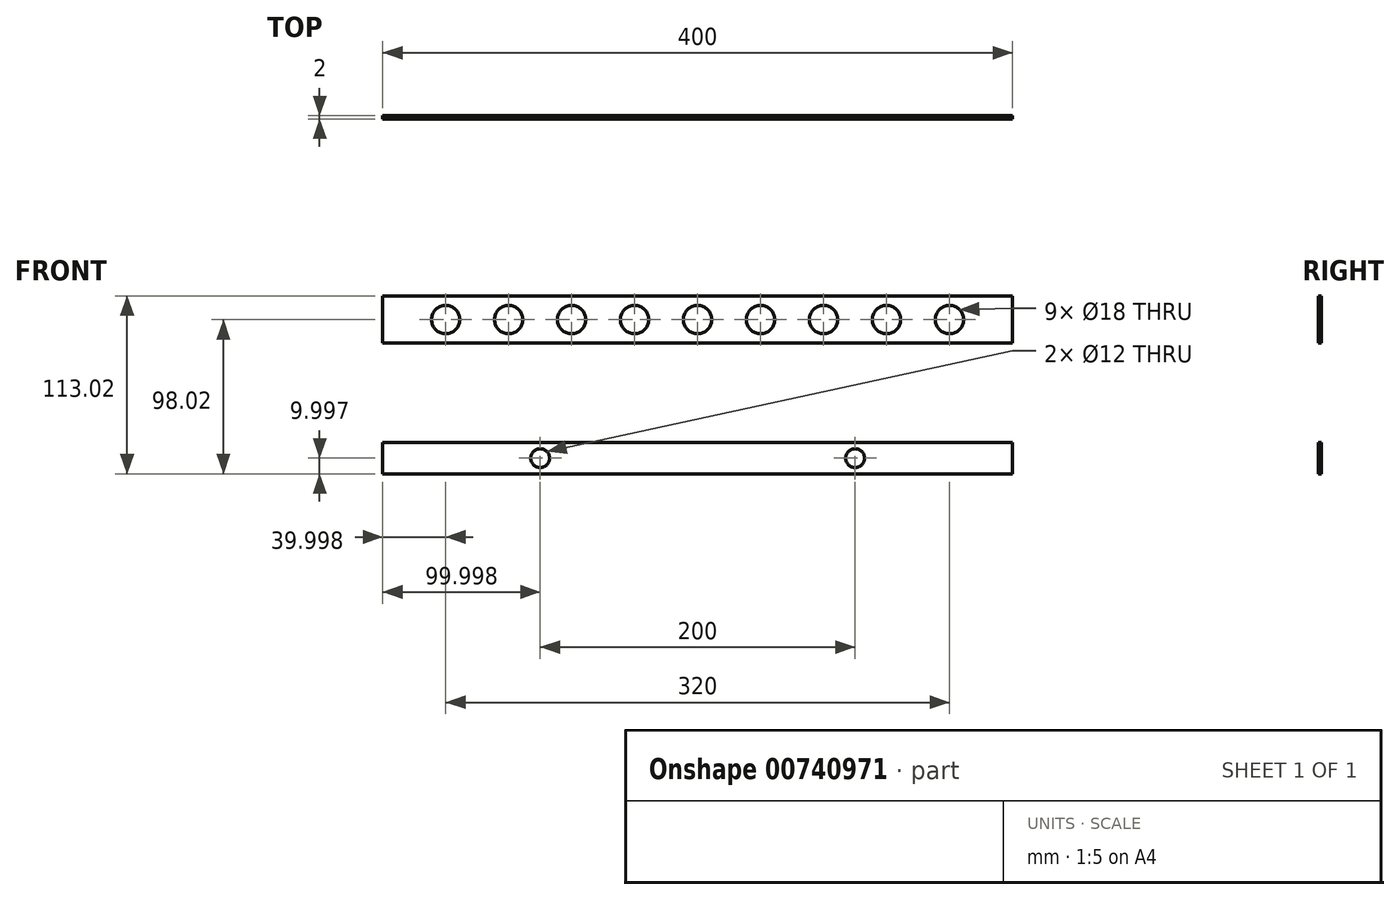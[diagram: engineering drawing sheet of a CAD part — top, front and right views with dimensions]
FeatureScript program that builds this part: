
annotation { "Feature Type Name" : "Feature", "Feature Type Description" : "" }
export const myFeature = defineFeature(function(context is Context, id is Id, definition is map)
    precondition{}
    {
        {
            var Q0;
            Q0=qCreatedBy(makeId("Front.planeOp"),FACE);
            var sketch = newSketch(context, id + "F0", { "sketchPlane" : qUnion([Q0])});
            skCircle(sketch, "E0", {"center": v(-57.63, 0) * mm, "radius": 9 * mm});
            skCircle(sketch, "E1.1.0.0", {"center": v(-17.63, 0) * mm, "radius": 9 * mm});
            skCircle(sketch, "E1.2.0.0", {"center": v(22.37, 0) * mm, "radius": 9 * mm});
            skCircle(sketch, "E1.3.0.0", {"center": v(62.37, 0) * mm, "radius": 9 * mm});
            skCircle(sketch, "E1.4.0.0", {"center": v(102.37, 0) * mm, "radius": 9 * mm});
            skCircle(sketch, "E1.5.0.0", {"center": v(142.37, 0) * mm, "radius": 9 * mm});
            skCircle(sketch, "E1.6.0.0", {"center": v(182.37, 0) * mm, "radius": 9 * mm});
            skCircle(sketch, "E1.7.0.0", {"center": v(222.37, 0) * mm, "radius": 9 * mm});
            skCircle(sketch, "E1.8.0.0", {"center": v(262.37, 0) * mm, "radius": 9 * mm});
            skLineSegment(sketch, "E1.direction1", {"start": v(-57.63, 0) * mm, "end": v(-17.63, 0) * mm, "construction": true});
            skLineSegment(sketch, "E2.bottom", {"start": v(-97.63, 15) * mm, "end": v(302.37, 15) * mm});
            skLineSegment(sketch, "E2.top", {"start": v(-97.63, -15) * mm, "end": v(302.37, -15) * mm});
            skLineSegment(sketch, "E2.left", {"start": v(-97.63, 15) * mm, "end": v(-97.63, -15) * mm});
            skLineSegment(sketch, "E2.right", {"start": v(302.37, 15) * mm, "end": v(302.37, -15) * mm});
            skLineSegment(sketch, "E3.bottom", {"start": v(-97.63, -78.02) * mm, "end": v(302.37, -78.02) * mm});
            skLineSegment(sketch, "E3.top", {"start": v(-97.63, -98.02) * mm, "end": v(302.37, -98.02) * mm});
            skLineSegment(sketch, "E3.left", {"start": v(-97.63, -78.02) * mm, "end": v(-97.63, -98.02) * mm});
            skLineSegment(sketch, "E3.right", {"start": v(302.37, -78.02) * mm, "end": v(302.37, -98.02) * mm});
            skCircle(sketch, "E4", {"center": v(2.37, -88.02) * mm, "radius": 6 * mm});
            skCircle(sketch, "E5.1.0.0", {"center": v(202.37, -88.02) * mm, "radius": 6 * mm});
            skLineSegment(sketch, "E5.direction1", {"start": v(2.37, -88.02) * mm, "end": v(202.37, -88.02) * mm, "construction": true});
            skCircle(sketch, "E6", {"center": v(-2185.26, 551.6) * mm, "radius": 8 * mm});
            skCircle(sketch, "E7.1.0.0", {"center": v(-2145.26, 551.6) * mm, "radius": 8 * mm});
            skCircle(sketch, "E7.2.0.0", {"center": v(-2105.26, 551.6) * mm, "radius": 8 * mm});
            skCircle(sketch, "E7.3.0.0", {"center": v(-2065.26, 551.6) * mm, "radius": 8 * mm});
            skCircle(sketch, "E7.4.0.0", {"center": v(-2025.26, 551.6) * mm, "radius": 8 * mm});
            skCircle(sketch, "E7.5.0.0", {"center": v(-1985.26, 551.6) * mm, "radius": 8 * mm});
            skCircle(sketch, "E7.6.0.0", {"center": v(-1945.26, 551.6) * mm, "radius": 8 * mm});
            skCircle(sketch, "E7.7.0.0", {"center": v(-1905.26, 551.6) * mm, "radius": 8 * mm});
            skCircle(sketch, "E7.8.0.0", {"center": v(-1865.26, 551.6) * mm, "radius": 8 * mm});
            skLineSegment(sketch, "E7.direction1", {"start": v(-2185.26, 551.6) * mm, "end": v(-2145.26, 551.6) * mm, "construction": true});
            skLineSegment(sketch, "E8.bottom", {"start": v(-2225.26, 568.6) * mm, "end": v(-1825.26, 568.6) * mm});
            skLineSegment(sketch, "E8.top", {"start": v(-2225.26, 538.6) * mm, "end": v(-1825.26, 538.6) * mm});
            skLineSegment(sketch, "E8.left", {"start": v(-2225.26, 568.6) * mm, "end": v(-2225.26, 538.6) * mm});
            skLineSegment(sketch, "E8.right", {"start": v(-1825.26, 568.6) * mm, "end": v(-1825.26, 538.6) * mm});
            skLineSegment(sketch, "E9.bottom", {"start": v(-2225.26, 472.57) * mm, "end": v(-1825.26, 472.57) * mm});
            skLineSegment(sketch, "E9.top", {"start": v(-2225.26, 442.57) * mm, "end": v(-1825.26, 442.57) * mm});
            skLineSegment(sketch, "E9.left", {"start": v(-2225.26, 472.57) * mm, "end": v(-2225.26, 442.57) * mm});
            skLineSegment(sketch, "E9.right", {"start": v(-1825.26, 472.57) * mm, "end": v(-1825.26, 442.57) * mm});
            skCircle(sketch, "E10", {"center": v(-2125.26, 463.57) * mm, "radius": 3 * mm});
            skCircle(sketch, "E11.1.0.0", {"center": v(-1925.26, 463.57) * mm, "radius": 3 * mm});
            skLineSegment(sketch, "E11.direction1", {"start": v(-2125.26, 463.57) * mm, "end": v(-1925.26, 463.57) * mm, "construction": true});
            skSolve(sketch);
        }
        {
            var Q0;
            Q0=makeQuery(id+"F0.imprint","IMPRINT",FACE,{"disambiguationData":[TD([[makeQuery(id+"F0.imprint","IMPRINT",EDGE,{"derivedFrom":sQuery(id+"F0.wireOp",EDGE,"E0")}),-1.0]])]});
            var Q1;
            Q1=makeQuery(id+"F0.imprint","IMPRINT",FACE,{"disambiguationData":[TD([[makeQuery(id+"F0.imprint","IMPRINT",EDGE,{"derivedFrom":sQuery(id+"F0.wireOp",EDGE,"E3.bottom")}),-1.0]])]});
            extrude(context, id + "F1", {"entities" : qUnion([Q0, Q1]), "depth" : 2 * mm, "offsetDistance" : 25 * mm});
        }
    });
